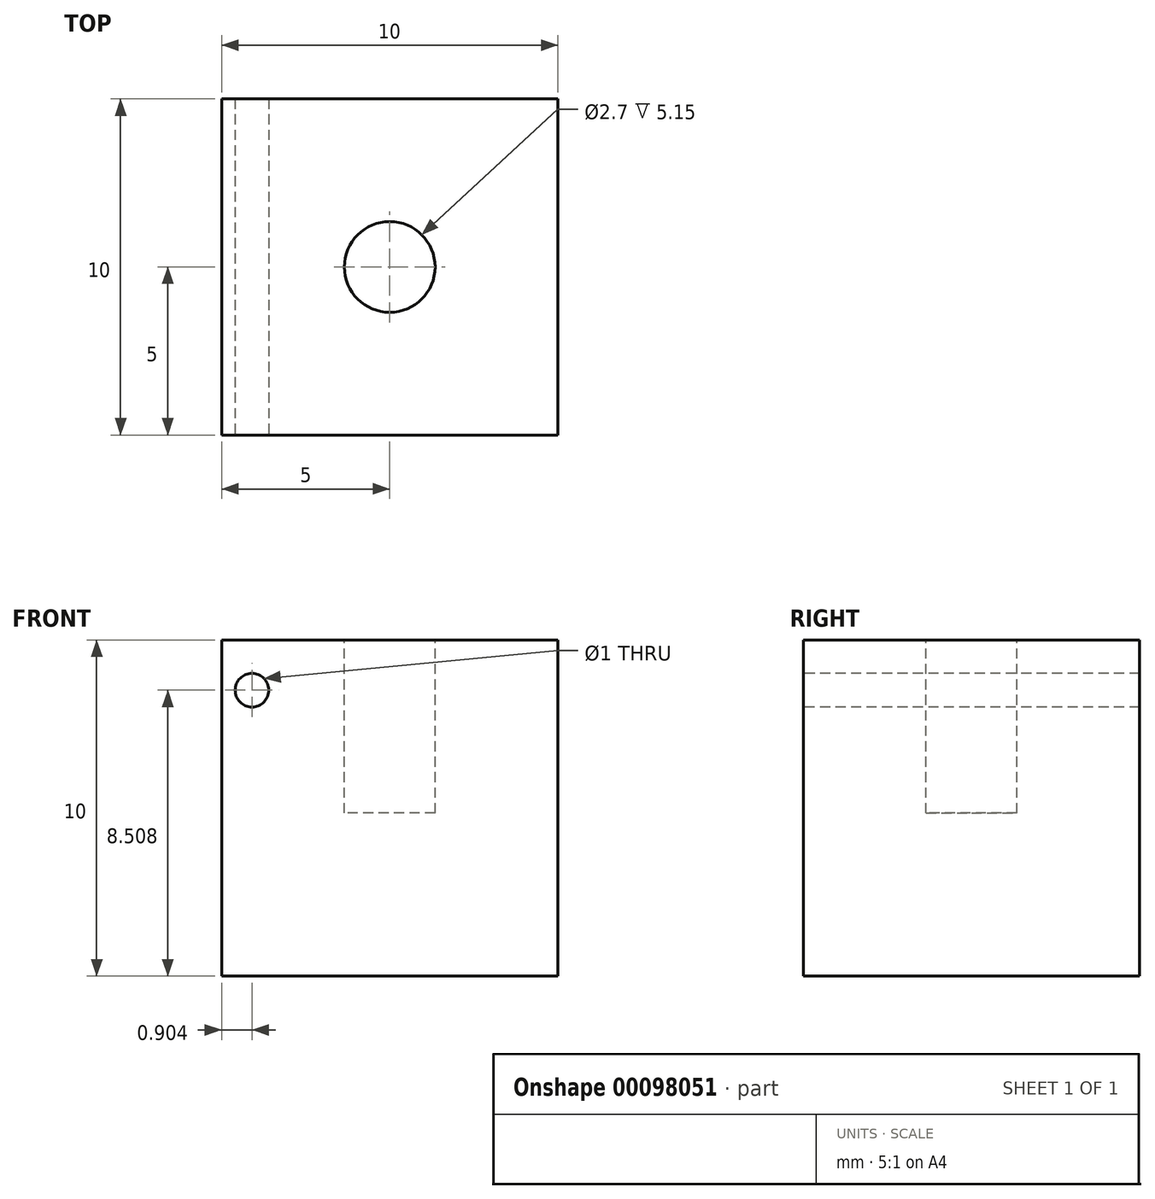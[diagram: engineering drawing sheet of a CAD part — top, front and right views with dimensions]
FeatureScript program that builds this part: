
annotation { "Feature Type Name" : "Feature", "Feature Type Description" : "" }
export const myFeature = defineFeature(function(context is Context, id is Id, definition is map)
    precondition{}
    {
        {
            var Q0;
            Q0=qCreatedBy(makeId("Top.planeOp"),FACE);
            var sketch = newSketch(context, id + "F0", { "sketchPlane" : qUnion([Q0])});
            skLineSegment(sketch, "E0.bottom", {"start": v(0, 0) * mm, "end": v(10, 0) * mm});
            skLineSegment(sketch, "E0.top", {"start": v(0, 10) * mm, "end": v(10, 10) * mm});
            skLineSegment(sketch, "E0.left", {"start": v(0, 0) * mm, "end": v(0, 10) * mm});
            skLineSegment(sketch, "E0.right", {"start": v(10, 0) * mm, "end": v(10, 10) * mm});
            skSolve(sketch);
        }
        {
            var Q0;
            Q0 = qSketchRegion(id + "F0", true);
            extrude(context, id + "F1", {"entities" : qUnion([Q0]), "depth" : 10 * mm});
        }
        {
            var Q0;
            Q0=makeQuery(id+"F1.opExtrude","CAP_FACE",FACE,{"disambiguationData":[OSD([sQuery(id+"F0.wireOp",EDGE,"E0.bottom"),sQuery(id+"F0.wireOp",EDGE,"E0.top"),sQuery(id+"F0.wireOp",EDGE,"E0.left"),sQuery(id+"F0.wireOp",EDGE,"E0.right")])],"isStart":false});
            var sketch = newSketch(context, id + "F2", { "sketchPlane" : qUnion([Q0])});
            skCircle(sketch, "E1", {"center": v(5, 5) * mm, "radius": 1.35 * mm});
            skSolve(sketch);
        }
        {
            var Q0;
            Q0 = qSketchRegion(id + "F2", true);
            extrude(context, id + "F3", {"entities" : qUnion([Q0]), "operationType" : NewBodyOperationType.REMOVE, "oppositeDirection" : true, "depth" : 5.15 * mm});
        }
        {
            var Q0;
            Q0=makeQuery(id+"F1.opExtrude","SWEPT_FACE",FACE,{"disambiguationData":[OSD([sQuery(id+"F0.wireOp",EDGE,"E0.bottom")])]});
            var sketch = newSketch(context, id + "F4", { "sketchPlane" : qUnion([Q0])});
            skCircle(sketch, "E2", {"center": v(0.9, 8.5) * mm, "radius": 0.5 * mm});
            skSolve(sketch);
        }
        {
            var Q0;
            Q0 = qSketchRegion(id + "F4", true);
            extrude(context, id + "F5", {"entities" : qUnion([Q0]), "operationType" : NewBodyOperationType.REMOVE, "endBound" : BoundingType.THROUGH_ALL, "oppositeDirection" : true, "depth" : 25 * mm});
        }
    });
